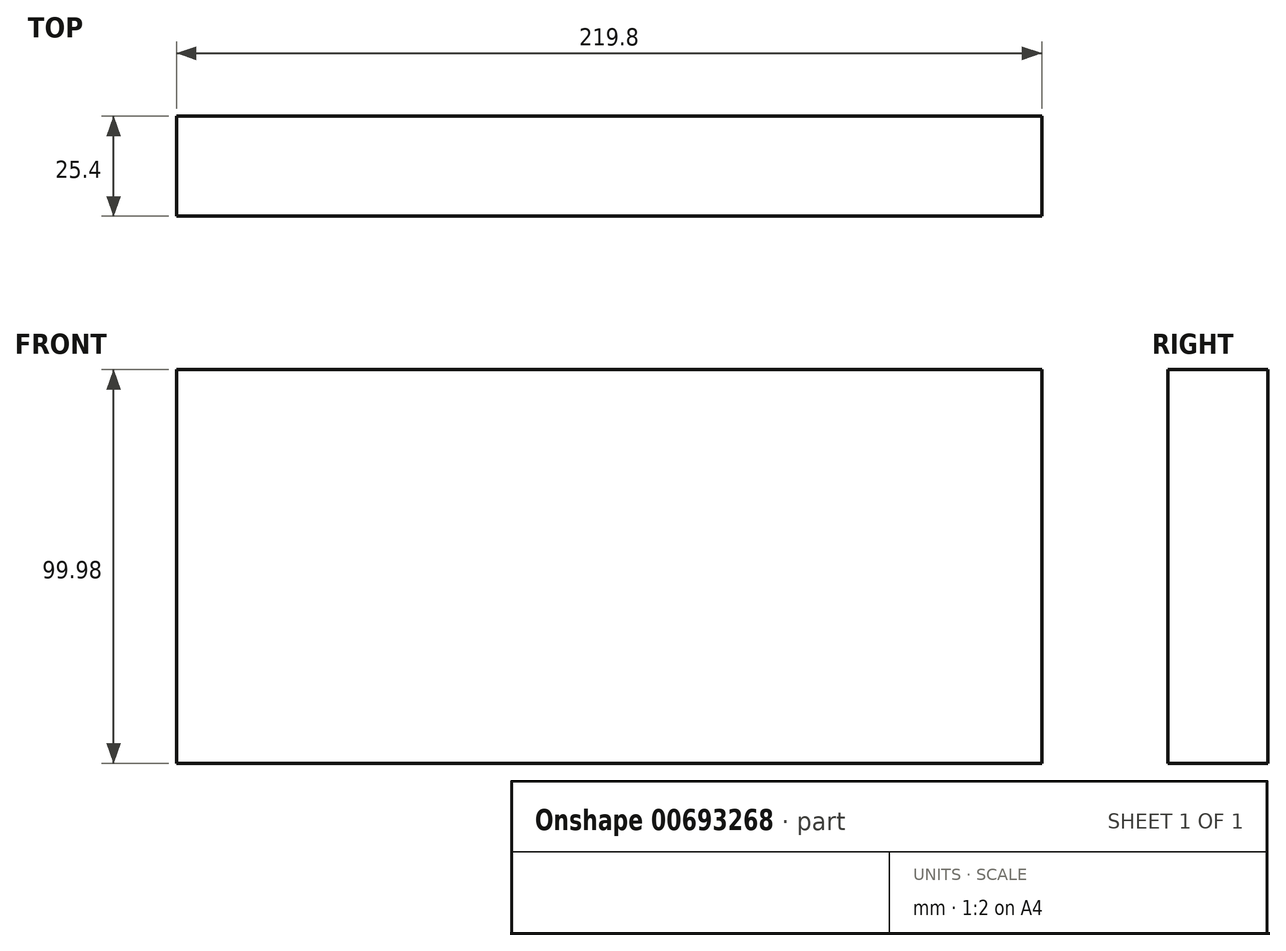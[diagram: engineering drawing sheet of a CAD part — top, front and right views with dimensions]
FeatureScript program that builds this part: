
annotation { "Feature Type Name" : "Feature", "Feature Type Description" : "" }
export const myFeature = defineFeature(function(context is Context, id is Id, definition is map)
    precondition{}
    {
        {
            var Q0;
            Q0=qCreatedBy(makeId("Front.planeOp"),FACE);
            var sketch = newSketch(context, id + "F0", { "sketchPlane" : qUnion([Q0])});
            skLineSegment(sketch, "E0.bottom", {"start": v(109.9, -49.99) * mm, "end": v(-109.9, -49.99) * mm});
            skLineSegment(sketch, "E0.top", {"start": v(109.9, 49.99) * mm, "end": v(-109.9, 49.99) * mm});
            skLineSegment(sketch, "E0.left", {"start": v(109.9, -49.99) * mm, "end": v(109.9, 49.99) * mm});
            skLineSegment(sketch, "E0.right", {"start": v(-109.9, -49.99) * mm, "end": v(-109.9, 49.99) * mm});
            skPoint(sketch, "E0.middle", {"position": v(0, 0) * mm});
            skSolve(sketch);
        }
        {
            var Q0;
            Q0=makeQuery(id+"F0.imprint","IMPRINT",FACE,{"disambiguationData":[TD([[makeQuery(id+"F0.imprint","IMPRINT",EDGE,{"derivedFrom":sQuery(id+"F0.wireOp",EDGE,"E0.bottom")}),-1.0]])]});
            extrude(context, id + "F1", {"entities" : qUnion([Q0]), "depth" : 25.4 * mm, "offsetDistance" : 25.4 * mm});
        }
    });
